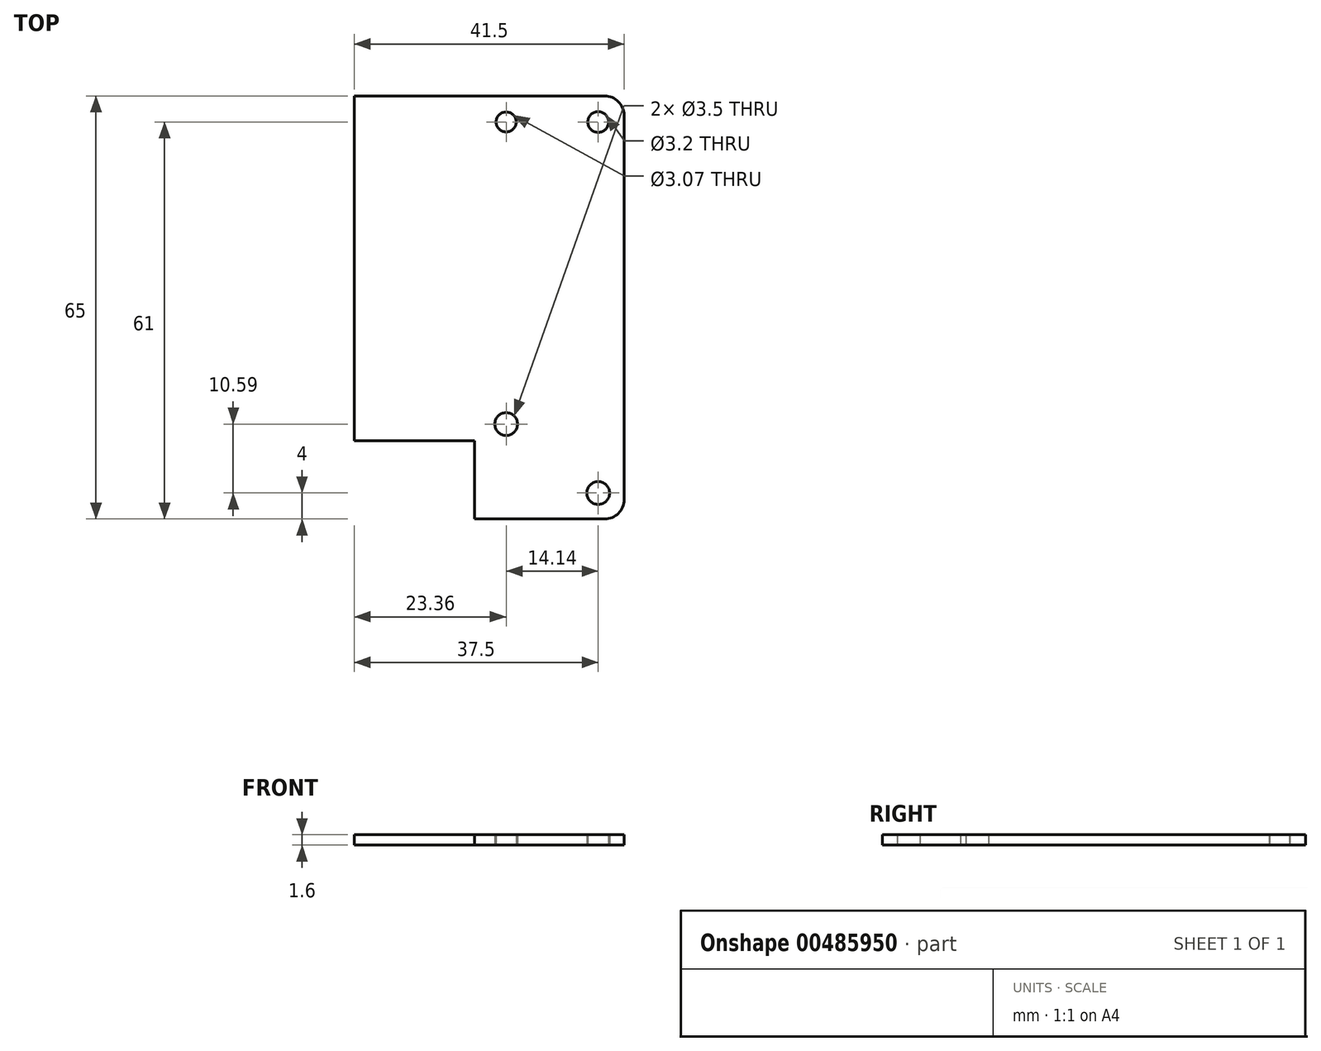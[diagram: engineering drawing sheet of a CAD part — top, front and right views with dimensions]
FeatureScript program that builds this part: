
annotation { "Feature Type Name" : "Feature", "Feature Type Description" : "" }
export const myFeature = defineFeature(function(context is Context, id is Id, definition is map)
    precondition{}
    {
        {
            var Q0;
            Q0=qCreatedBy(makeId("Top.planeOp"),FACE);
            var sketch = newSketch(context, id + "F0", { "sketchPlane" : qUnion([Q0])});
            skLineSegment(sketch, "E0", {"start": v(0, 0) * mm, "end": v(20, 0) * mm});
            skLineSegment(sketch, "E1", {"start": v(23, 3) * mm, "end": v(23, 62) * mm});
            skLineSegment(sketch, "E2", {"start": v(20, 65) * mm, "end": v(-18.5, 65) * mm});
            skLineSegment(sketch, "E3", {"start": v(-18.5, 65) * mm, "end": v(-18.5, 12) * mm});
            skLineSegment(sketch, "E4", {"start": v(-18.5, 12) * mm, "end": v(0, 12) * mm});
            skLineSegment(sketch, "E5", {"start": v(0, 12) * mm, "end": v(0, 0) * mm});
            skPoint(sketch, "E6.visualSharp", {"position": v(23, 0) * mm});
            skArc(sketch, "E6.filletArc", {"start": v(20, 0) * mm, "mid": v(22.12, 0.88) * mm, "end": v(23, 3) * mm});
            skPoint(sketch, "E7.visualSharp", {"position": v(23, 65) * mm});
            skArc(sketch, "E7.filletArc", {"start": v(23, 62) * mm, "mid": v(22.12, 64.12) * mm, "end": v(20, 65) * mm});
            skCircle(sketch, "E8", {"center": v(19, 61) * mm, "radius": 1.6 * mm});
            skCircle(sketch, "E9", {"center": v(19, 4) * mm, "radius": 1.75 * mm});
            skCircle(sketch, "E10", {"center": v(4.86, 14.59) * mm, "radius": 1.75 * mm});
            skCircle(sketch, "E11", {"center": v(4.86, 61) * mm, "radius": 1.54 * mm});
            skSolve(sketch);
        }
        {
            var Q0;
            Q0 = qSketchRegion(id + "F0", true);
            extrude(context, id + "F1", {"entities" : qUnion([Q0]), "depth" : 1.6 * mm});
        }
    });
